# Revit family: Mailboxes_4C-Salsbury_Industries-Surface_Mounted-14_Door_High_Units
name_source: partatom
category: Specialty Equipment
revit_build: Autodesk Revit 2016 (Build: 20150714_1515(x64)
units: mm (PartAtom-declared; Revit-internal decimal feet)

## family parameters
Always vertical = Yes
Cut with Voids When Loaded = No
OmniClass Number = 23.40.90.14.11
OmniClass Title = Mail Boxes
Part Type = Normal
Room Calculation Point = No
Round Connector Dimension = Use Diameter
Shared = No
Work Plane-Based = No

## types (14) — shared parameters
4C Unit Elevation = 13.683 "
4C Unit Height = 51.5 "
Above Finished Floor (Bottom of Unit) = 13.12 "
Assembly Code = C1030910
Assembly Description = Mailboxes
Depth = 17.5 "
Height = 52.594 "
Lock Material = Stainless Steel - Salsbury Finish -  Polished
Manufacturer = Salsbury Industries
MasterFormat Number = 10 55 00
MasterFormat Title = Postal Specialties
OmniClass 23 Number = 23.40.90.14.11
OmniClass 23 Title = Mail Boxes
Type Comments = Surface Mounted 4C Horizontal Mailboxes - Front Loading
URL = www.mailboxes.com
Version = 1.0 (06/30/17)

## per-type parameters (varying)
| type | 4C Unit | Description | Width |
| 3814S-12 | Mailboxes_4C-Salsbury_Industries-Front_Load-14_Door_High_Units : 3714S-12 FL | 14 Door High Unit:  12 MB1, OM2 | 17.496 " |
| 3814D-16 | Mailboxes_4C-Salsbury_Industries-Front_Load-14_Door_High_Units : 3714D-16 FL | 14 Door High Unit:  16 MB1, 2 PL5, OM2 | 32.25 " |
| 3814D-26 | Mailboxes_4C-Salsbury_Industries-Front_Load-14_Door_High_Units : 3714D-26 FL | 14 Door High Unit:  26 MB1, OM2 | 32.25 " |
| 3814D-15 | Mailboxes_4C-Salsbury_Industries-Front_Load-14_Door_High_Units : 3714D-15 FL | 14 Door High Unit:  15 MB1, 1 PL5, 1 PL6, OM2 | 32.25 " |
| 3814D-14 | Mailboxes_4C-Salsbury_Industries-Front_Load-14_Door_High_Units : 3714D-14 FL | 14 Door High Unit:  14 MB1, 2 PL6, OM2 | 32.25 " |
| 3814D-07 | Mailboxes_4C-Salsbury_Industries-Front_Load-14_Door_High_Units : 3714D-07 FL | 14 Door High Unit:  7 MB2, 2 PL6, OM2 | 32.25 " |
| 3814D-13 | Mailboxes_4C-Salsbury_Industries-Front_Load-14_Door_High_Units : 3714D-13 FL | 14 Door High Unit:  13 MB2, OM2 | 32.25 " |
| 3814S-07 | Mailboxes_4C-Salsbury_Industries-Front_Load-14_Door_High_Units : 3714S-07 FL | 14 Door High Unit:  7 MB1, 1 PL5, OM2 | 17.496 " |
| 3814S-03 | Mailboxes_4C-Salsbury_Industries-Front_Load-14_Door_High_Units : 3714S-03 FL | 14 Door High Unit:  3 MB2, 1 PL6, OM2 | 17.496 " |
| 3814S-3P | Mailboxes_4C-Salsbury_Industries-Front_Load-14_Door_High_Units : 3714S-3P FL | 14 Door High Unit:  1 PL4, 2 PL5 | 17.496 " |
| 3814S-2P | Mailboxes_4C-Salsbury_Industries-Front_Load-14_Door_High_Units : 3714S-2P FL | 14 Door High Unit:  2 PL6, OM2 | 17.496 " |
| 3814S-06 | Mailboxes_4C-Salsbury_Industries-Front_Load-14_Door_High_Units : 3714S-06 FL | 14 Door High Unit:  6 MB2, OM2 | 17.496 " |
| 3814S-2B | Mailboxes_4C-Salsbury_Industries-Front_Load-14_Door_High_Units : 3714S-2B FL | 14 Door High Unit:  2 Receptacle Bins | 17.496 " |
| 3814S-1C | Mailboxes_4C-Salsbury_Industries-Front_Load-14_Door_High_Units : 3714S-1C FL | 14 Door High Unit:  1 Collection Box | 17.496 " |

note: column(s) folded — value = type name in every type: Model

## geometry (parser evidence)
native form markers: Blend x6, Extrusion x4, Sweep x13
no freeform markers — native parametric forms only
